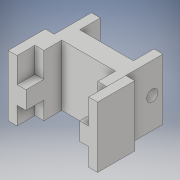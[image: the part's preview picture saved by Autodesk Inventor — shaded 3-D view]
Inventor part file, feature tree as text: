
AUTODESK INVENTOR PART (.ipt)
format: ipt  version: 2017 (Build 210142000, 142)  size: 192,000 bytes
history: native  units: in
note: dims shown in document units (in); Inventor stores cm internally (conversion verified against a paired STEP export)
features: sketch x8, extrude x7, hole x1
ambient origin geometry x8: Origin, YZ Plane, XZ Plane, XY Plane, X Axis, Y Axis, Z Axis, Center Point
bodies: Solid1 (feature_tree)
feature tree (16):
  extrude  "Extrusion1"  Depth=1.7in
  extrude  "Extrusion2"  TaperAngle=0.0deg  [1 undecoded]
  extrude  "Extrusion3"  Depth=0.7in
  extrude  "Extrusion4"  TaperAngle=0.0deg  [1 undecoded]
  extrude  "Extrusion5"  Depth=0.25in
  hole  "Hole2"  [1 undecoded]
  extrude  "Extrusion8"  Depth=0.5in
  extrude  "Extrusion9"  Depth=1.7in TaperAngle=0.0deg
  sketch  "Sketch1"  dims[d0=2.075in d1=1.7in]
  sketch  "Sketch2"  dims[d2=2.0in d3=0.0in d4=0.0in]
  sketch  "Sketch3"  dims[d5=0.5in d6=0.7in]
  sketch  "Sketch4"  dims[d8=0.0in d9=0.0in d10=0.0in]
  sketch  "Sketch5"  dims[d12=0.25in d13=0.25in]
  sketch  "Sketch9"  dims[d14=0.25in d15=0.0in]
  sketch  "Sketch10"  dims[d16=0.0in d17=0.0in d22=0.5in]
  sketch  "Sketch11"  dims[d23=0.5in d24=1.7in d25=0.0in d26=0.0in d28=0.0in d29=0.0in d30=1.7in d31=0.0in d32=0.5in d33=0.5in d49=0.3in d50=0.85in d51=0.85in d52=0.31in d53=0.75in d54=0.375in d55=0.25in d56=0.5635in d57=1.0in d58=0.8108in d59=0.0in d60=1.0375in d61=0.25in d62=0.0in d63=1.0375in d64=0.25in d65=0.0in]
note: 3 required parameter values undecoded (feature->parameter linkage not recoverable at this tier; creation-order binding heuristic only, values carry confidence <= 0.55)
